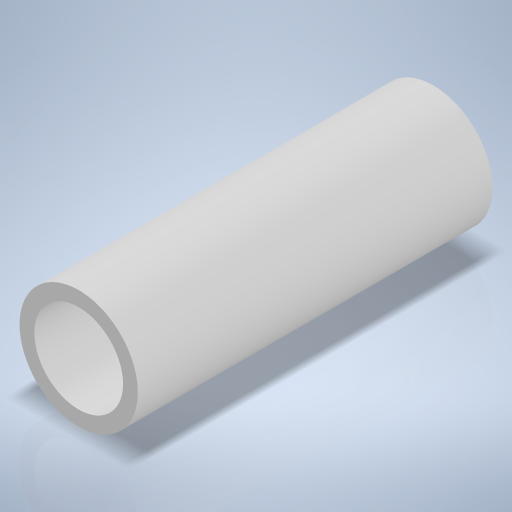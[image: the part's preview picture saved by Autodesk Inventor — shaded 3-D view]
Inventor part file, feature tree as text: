
AUTODESK INVENTOR PART (.ipt)
format: ipt  version: 2024 (Build 280153000, 153)  size: 220,160 bytes
history: native  units: mm
features: extrude x1, sketch x1
ambient origin geometry x8: Origin, YZ Plane, XZ Plane, XY Plane, X Axis, Y Axis, Z Axis, Center Point
bodies: Volumenkörper1 (feature_tree)
feature tree (2):
  extrude  "Extrusion1"  Depth=18.0mm
  sketch  "Skizze1"  dims[d0=6.0mm d1=4.5mm d2=18.0mm d3=0.0mm]
